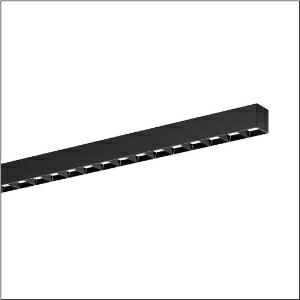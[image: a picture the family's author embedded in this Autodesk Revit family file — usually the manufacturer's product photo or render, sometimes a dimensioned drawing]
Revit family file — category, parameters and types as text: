
# Revit family: silica_r__21_51mx22dc4abb_087a
name_source: partatom
category: Lighting Fixtures
units: mm (PartAtom-declared; Revit-internal decimal feet)

## family parameters
Cut with Voids When Loaded = No
Host = Face
Light Source = No
Part Type = Normal
Room Calculation Point = No
Round Connector Dimension = Use Diameter
Shared = No

## types (1)
- --- (1 x LED, 10800 lm, 64.7 W, 4000K)
    Apparent Load = 65 VA
    CIE Flux Codes = 86 100 100 100 100
    Color Rendering = 80
    Color Temperature = 4000K
    Default Elevation = 1800 mm
    Description = Silica® 21, office luminaire, primary light control with darklight reflector, of PMMA, black, CAT 2 (L<= 3000cd/m²), light emission: direct distribution, primary light characteristic: symmetric, installation type: surface-mounted, LED, rated luminous flux: 10.800lm, luminous efficacy: 167lm/W, light colour: 840, colour temperature: 4000K, with terminal, 3+2-pole, max. 2.5mm², mains connection: 220..240V, AC, 50/60Hz, rated input power: 64.7W, luminaire housing, of aluminium, jet black (RAL 9005), length: 3.004mm, width: 53mm, height: 53mm, protection rating (complete): IP20, insulation class (complete): insulation class I (protective earthing), certification: CE, permissible operating ambient temperature: 0..+35°C, standard: EN 50419, packaging unit: 1 piece
    Height = 0 mm  [stored 0 ft]
    Lamp = 1 x LED
    Lamp Light Flux = 10800 lm
    Lamp Power = 64.7 W
    Lamp count = 1
    Length = 3004 mm
    Luminous efficacy = 167 lm/W
    Manufacturer = Siteco
    ModVariant = No
    Model = 51MX22DC4ABB
    Mounting Place = Ceiling
    Mounting Type = Recessed
    Number of Poles = 1
    OnlyDefault = Yes
    Power Factor = 1
    Product Name = Silica® 21
    Product group = office luminaire | ceiling recessed
    ProductGroupID = 400
    Protection Class = Protection class I
    Protection Degree = IP 20
    RLX_Detail_Level = 1
    RLX_Emergency_Light_Flux = 0 lm
    RLX_Emergency_Type = 0
    RLX_Emergency_Type_DB = No
    RlxData = <blob elided: 64465 chars, md5=722b0d15>
    Socket = socket
    Standby Power = 0 W
    System Light Flux = 10800 lm
    System Power = 65 W
    Type Comments = factory setting: luminous flux: 100 % | dim-lin: 254 | 366 mA
    Type Image = l_1335908.jpg
    URL = http://relux.com
    VarID = @adj_094889
    Voltage = 0 V
    Weight = 0.00 kg
    Width = 53 mm

note: [stored X ft] marks values corroborated as IEEE doubles in the binary element streams (Revit-internal decimal feet)

## geometry (parser evidence)
native form markers: Blend x4, Sweep x10
no freeform markers — native parametric forms only
